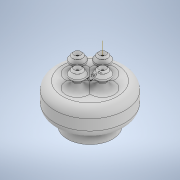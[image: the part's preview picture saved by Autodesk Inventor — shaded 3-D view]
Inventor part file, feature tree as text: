
AUTODESK INVENTOR PART (.ipt)
format: ipt  version: 2020 (Build 240168000, 168)  size: 352,256 bytes
history: native  units: in
note: dims shown in document units (in); Inventor stores cm internally (conversion verified against a paired STEP export)
features: sketch x4, revolve x3, fillet x2, other x1, pattern_circular x1
ambient origin geometry x8: Origin, YZ Plane, XZ Plane, XY Plane, X Axis, Y Axis, Z Axis, Center Point
bodies: Solid1 (feature_tree)
feature tree (11):
  revolve  "Revolution1"  [1 undecoded]
  sketch  "Sketch2"  dims[d2=0.2165in d3=0.0787in]
  other  "Work Axis1"
  revolve  "Revolution2"  [1 undecoded]
  sketch  "Sketch4"  dims[d6=0.1181in d7=0.1181in d9=90.0deg d10=0.1969in d11=0.0197in d12=0.1181in d13=0.0in d14=0.0787in d15=135.0deg d16=0.0787in d17=0.0492in d18=0.0394in d20=90.0deg d26=90.0deg d30=0.0787in d31=0.125in d32=0.0197in d33=90.0deg d34=1.5748in d35=360.0deg]
  revolve  "Revolution3"  [1 undecoded]
  pattern_circular  "Circular Pattern2"  [2 undecoded]
  fillet  "Fillet1"  [1 undecoded]
  fillet  "Fillet2"  Radius=0.1969in
  sketch  "Sketch1"  dims[d0=0.1575in d1=0.2362in]
  sketch  "Sketch3"  dims[d4=0.1969in d5=0.1969in]
note: 6 required parameter values undecoded (feature->parameter linkage not recoverable at this tier; creation-order binding heuristic only, values carry confidence <= 0.55)